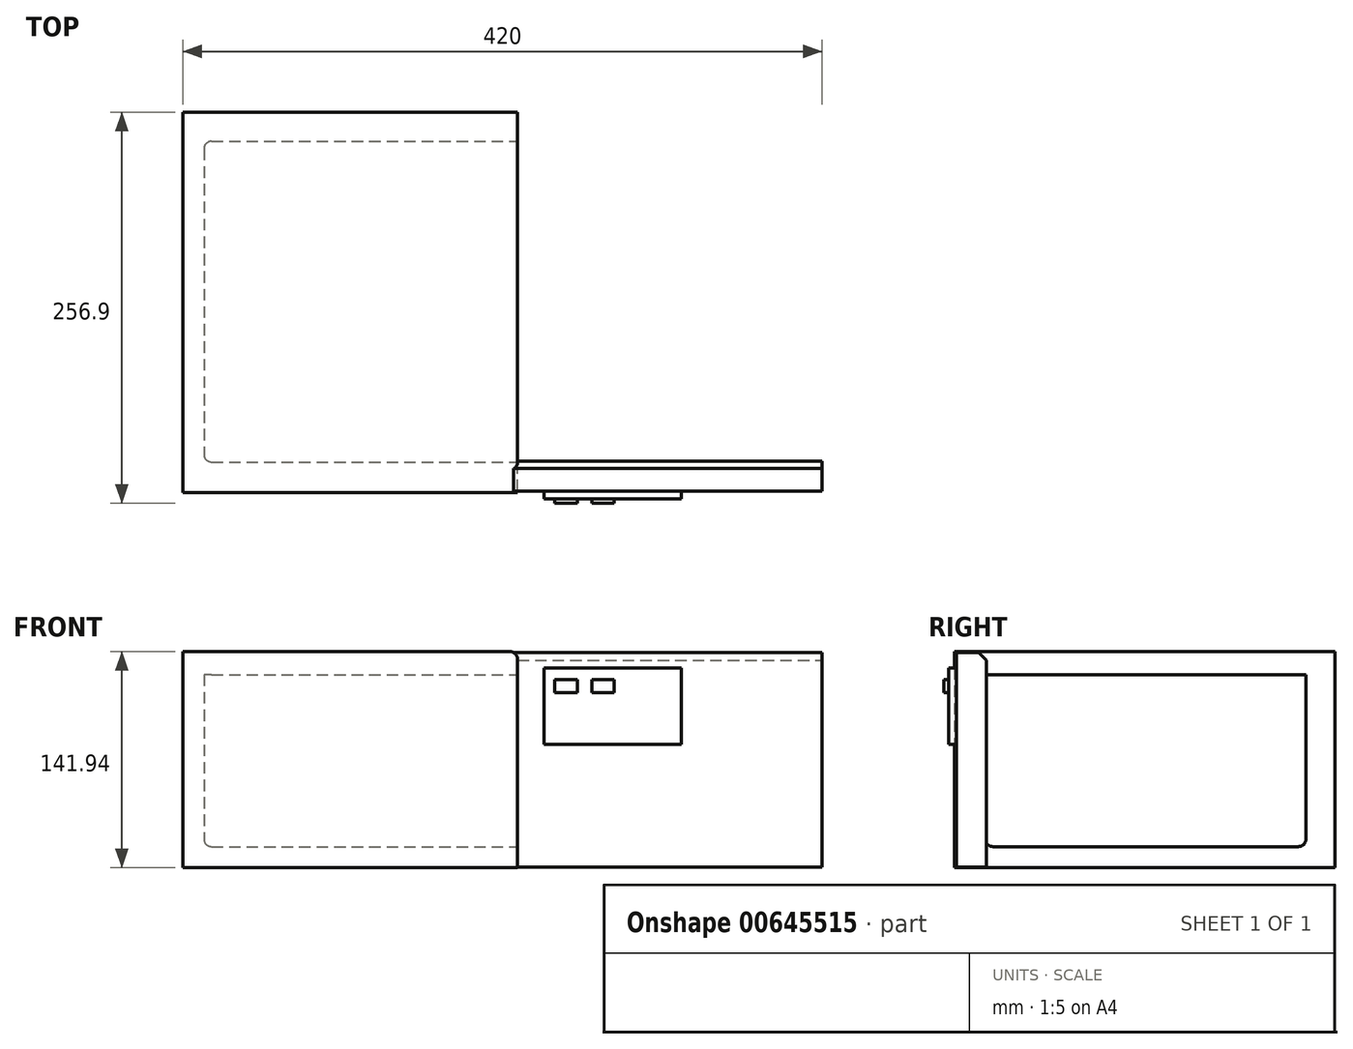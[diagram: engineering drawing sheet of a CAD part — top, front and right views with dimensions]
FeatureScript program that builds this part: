
annotation { "Feature Type Name" : "Feature", "Feature Type Description" : "" }
export const myFeature = defineFeature(function(context is Context, id is Id, definition is map)
    precondition{}
    {
        {
            var Q0;
            Q0=qCreatedBy(makeId("Front.planeOp"),FACE);
            var sketch = newSketch(context, id + "F0", { "sketchPlane" : qUnion([Q0])});
            skLineSegment(sketch, "E0.bottom", {"start": v(-110, 70.97) * mm, "end": v(110, 70.97) * mm});
            skLineSegment(sketch, "E0.top", {"start": v(-110, -70.97) * mm, "end": v(110, -70.97) * mm});
            skLineSegment(sketch, "E0.left", {"start": v(-110, 70.97) * mm, "end": v(-110, -70.97) * mm});
            skLineSegment(sketch, "E0.right", {"start": v(110, 70.97) * mm, "end": v(110, -70.97) * mm});
            skPoint(sketch, "E0.middle", {"position": v(0, 0) * mm});
            skSolve(sketch);
        }
        {
            var Q0;
            Q0=makeQuery(id+"F0.imprint","IMPRINT",FACE,{"disambiguationData":[TD([[makeQuery(id+"F0.imprint","IMPRINT",EDGE,{"derivedFrom":sQuery(id+"F0.wireOp",EDGE,"E0.bottom")}),-1.0]])]});
            extrude(context, id + "F1", {"entities" : qUnion([Q0]), "depth" : 250 * mm, "offsetDistance" : 25 * mm});
        }
        {
            var Q0;
            Q0=makeQuery(id+"F1.opExtrude","SWEPT_FACE",FACE,{"disambiguationData":[OSD([sQuery(id+"F0.wireOp",EDGE,"E0.right")])]});
            var sketch = newSketch(context, id + "F2", { "sketchPlane" : qUnion([Q0])});
            skSolve(sketch);
        }
        {
            var Q0;
            {var subQ0=sQuery(id+"F0.wireOp",EDGE,"E0.right");Q0=makeQuery(id+"F2.imprint","IMPRINT",FACE,{"disambiguationData":[TD([[makeQuery(id+"F2.imprint","IMPRINT",EDGE,{"derivedFrom":makeQuery(id+"F1.opExtrude","CAP_EDGE",EDGE,{"disambiguationData":[OSD([subQ0])],"isStart":true})}),-1.0]])]});}
            var sketch = newSketch(context, id + "F3", { "sketchPlane" : qUnion([Q0])});
            skLineSegment(sketch, "E1.bottom", {"start": v(-19.14, 55.88) * mm, "end": v(-229.82, 55.88) * mm});
            skLineSegment(sketch, "E1.top", {"start": v(-19.14, -57.12) * mm, "end": v(-229.82, -57.12) * mm});
            skLineSegment(sketch, "E1.left", {"start": v(-19.14, 55.88) * mm, "end": v(-19.14, -57.12) * mm});
            skLineSegment(sketch, "E1.right", {"start": v(-229.82, 55.88) * mm, "end": v(-229.82, -57.12) * mm});
            skSolve(sketch);
        }
        {
            var Q0;
            Q0 = qSketchRegion(id + "F3", true);
            extrude(context, id + "F4", {"entities" : qUnion([Q0]), "operationType" : NewBodyOperationType.REMOVE, "oppositeDirection" : true, "depth" : 206 * mm, "offsetDistance" : 25 * mm});
        }
        {
            var Q0;
            {var subQ0=sQuery(id+"F0.wireOp",EDGE,"E0.right");Q0=makeQuery(id+"F2.imprint","IMPRINT",FACE,{"disambiguationData":[TD([[makeQuery(id+"F2.imprint","IMPRINT",EDGE,{"derivedFrom":makeQuery(id+"F1.opExtrude","CAP_EDGE",EDGE,{"disambiguationData":[OSD([subQ0])],"isStart":true})}),-1.0]])]});}
            var sketch = newSketch(context, id + "F5", { "sketchPlane" : qUnion([Q0])});
            skLineSegment(sketch, "E2.bottom", {"start": v(-248.9, 70.32) * mm, "end": v(-229.11, 70.32) * mm});
            skLineSegment(sketch, "E2.top", {"start": v(-248.9, -70.68) * mm, "end": v(-229.11, -70.68) * mm});
            skLineSegment(sketch, "E2.left", {"start": v(-248.9, 70.32) * mm, "end": v(-248.9, -70.68) * mm});
            skLineSegment(sketch, "E2.right", {"start": v(-229.11, 70.32) * mm, "end": v(-229.11, -70.68) * mm});
            skSolve(sketch);
        }
        {
            var Q0;
            Q0 = qSketchRegion(id + "F5", true);
            extrude(context, id + "F6", {"entities" : qUnion([Q0]), "operationType" : NewBodyOperationType.ADD, "depth" : 200 * mm, "offsetDistance" : 25 * mm});
        }
        {
            var Q0;
            Q0=makeQuery(id+"F1.opExtrude","SWEPT_EDGE",EDGE,{"disambiguationData":[OSD([sQuery(id+"F0.wireOp",EDGE,"E0.bottom"),sQuery(id+"F0.wireOp",EDGE,"E0.right")])]});
            fillet(context, id + "F7", {"entities" : qUnion([Q0]), "radius" : 5 * mm, "tangentPropagation" : true, "allowEdgeOverflow" : false});
        }
        {
            var Q0;
            Q0=makeQuery(id+"F6.opExtrude","SWEPT_EDGE",EDGE,{"disambiguationData":[OSD([sQuery(id+"F5.wireOp",EDGE,"E2.bottom"),sQuery(id+"F5.wireOp",EDGE,"E2.right")])]});
            chamfer(context, id + "F8", {"entities" : qUnion([Q0]), "width" : 5 * mm, "tangentPropagation" : true});
        }
        {
            var Q0;
            Q0=makeQuery(id+"F4.boolean.opBoolean","COPY",EDGE,{"derivedFrom":makeQuery(id+"F4.opExtrude","SWEPT_EDGE",EDGE,{"disambiguationData":[OSD([sQuery(id+"F3.wireOp",EDGE,"E1.top"),sQuery(id+"F3.wireOp",EDGE,"E1.right")])]})});
            fillet(context, id + "F9", {"entities" : qUnion([Q0]), "radius" : 5 * mm, "tangentPropagation" : true, "allowEdgeOverflow" : false});
        }
        {
            var Q0;
            Q0=makeQuery(id+"F4.boolean.opBoolean","COPY",EDGE,{"derivedFrom":makeQuery(id+"F4.opExtrude","CAP_EDGE",EDGE,{"disambiguationData":[OSD([sQuery(id+"F3.wireOp",EDGE,"E1.top")])],"isStart":false})});
            fillet(context, id + "F10", {"entities" : qUnion([Q0]), "radius" : 5 * mm, "tangentPropagation" : true, "allowEdgeOverflow" : false});
        }
        {
            var Q0;
            Q0=makeQuery(id+"F4.boolean.opBoolean","COPY",EDGE,{"derivedFrom":makeQuery(id+"F4.opExtrude","SWEPT_EDGE",EDGE,{"disambiguationData":[OSD([sQuery(id+"F3.wireOp",EDGE,"E1.top"),sQuery(id+"F3.wireOp",EDGE,"E1.left")])]})});
            fillet(context, id + "F11", {"entities" : qUnion([Q0]), "radius" : 5 * mm, "tangentPropagation" : true, "allowEdgeOverflow" : false});
        }
        {
            var Q0;
            Q0=makeQuery(id+"F6.opExtrude","SWEPT_FACE",FACE,{"disambiguationData":[OSD([sQuery(id+"F5.wireOp",EDGE,"E2.left")])]});
            var sketch = newSketch(context, id + "F12", { "sketchPlane" : qUnion([Q0])});
            skLineSegment(sketch, "E3.bottom", {"start": v(127.43, 60.14) * mm, "end": v(217.43, 60.14) * mm});
            skLineSegment(sketch, "E3.top", {"start": v(127.43, 10.14) * mm, "end": v(217.43, 10.14) * mm});
            skLineSegment(sketch, "E3.left", {"start": v(127.43, 60.14) * mm, "end": v(127.43, 10.14) * mm});
            skLineSegment(sketch, "E3.right", {"start": v(217.43, 60.14) * mm, "end": v(217.43, 10.14) * mm});
            skSolve(sketch);
        }
        {
            var Q0;
            Q0 = qSketchRegion(id + "F12", true);
            extrude(context, id + "F13", {"entities" : qUnion([Q0]), "operationType" : NewBodyOperationType.ADD, "depth" : 5 * mm, "offsetDistance" : 25 * mm});
        }
        {
            var Q0;
            Q0=makeQuery(id+"F13.opExtrude","CAP_FACE",FACE,{"disambiguationData":[OSD([sQuery(id+"F12.wireOp",EDGE,"E3.bottom"),sQuery(id+"F12.wireOp",EDGE,"E3.top"),sQuery(id+"F12.wireOp",EDGE,"E3.left"),sQuery(id+"F12.wireOp",EDGE,"E3.right")])],"isStart":false});
            var sketch = newSketch(context, id + "F14", { "sketchPlane" : qUnion([Q0])});
            skLineSegment(sketch, "E4.bottom", {"start": v(134.4, 52.66) * mm, "end": v(149.18, 52.66) * mm});
            skLineSegment(sketch, "E4.top", {"start": v(134.4, 44.16) * mm, "end": v(149.18, 44.16) * mm});
            skLineSegment(sketch, "E4.left", {"start": v(134.4, 52.66) * mm, "end": v(134.4, 44.16) * mm});
            skLineSegment(sketch, "E4.right", {"start": v(149.18, 52.66) * mm, "end": v(149.18, 44.16) * mm});
            skSolve(sketch);
        }
        {
            var Q0;
            Q0 = qSketchRegion(id + "F14", true);
            extrude(context, id + "F15", {"entities" : qUnion([Q0]), "operationType" : NewBodyOperationType.ADD, "depth" : 3 * mm, "offsetDistance" : 25 * mm});
        }
        {
            var Q0;
            Q0=makeQuery(id+"F13.opExtrude","CAP_FACE",FACE,{"disambiguationData":[OSD([sQuery(id+"F12.wireOp",EDGE,"E3.bottom"),sQuery(id+"F12.wireOp",EDGE,"E3.top"),sQuery(id+"F12.wireOp",EDGE,"E3.left"),sQuery(id+"F12.wireOp",EDGE,"E3.right")])],"isStart":false});
            var sketch = newSketch(context, id + "F16", { "sketchPlane" : qUnion([Q0])});
            skPoint(sketch, "E5.oppositeSnap0", {"position": v(141.8, 44.16) * mm});
            skLineSegment(sketch, "E5.bottom", {"start": v(158.81, 52.66) * mm, "end": v(173.31, 52.66) * mm});
            skLineSegment(sketch, "E5.top", {"start": v(158.81, 44.16) * mm, "end": v(173.31, 44.16) * mm});
            skLineSegment(sketch, "E5.left", {"start": v(158.81, 52.66) * mm, "end": v(158.81, 44.16) * mm});
            skLineSegment(sketch, "E5.right", {"start": v(173.31, 52.66) * mm, "end": v(173.31, 44.16) * mm});
            skSolve(sketch);
        }
        {
            var Q0;
            Q0 = qSketchRegion(id + "F16", true);
            extrude(context, id + "F17", {"entities" : qUnion([Q0]), "operationType" : NewBodyOperationType.ADD, "depth" : 3 * mm, "offsetDistance" : 25 * mm});
        }
    });
